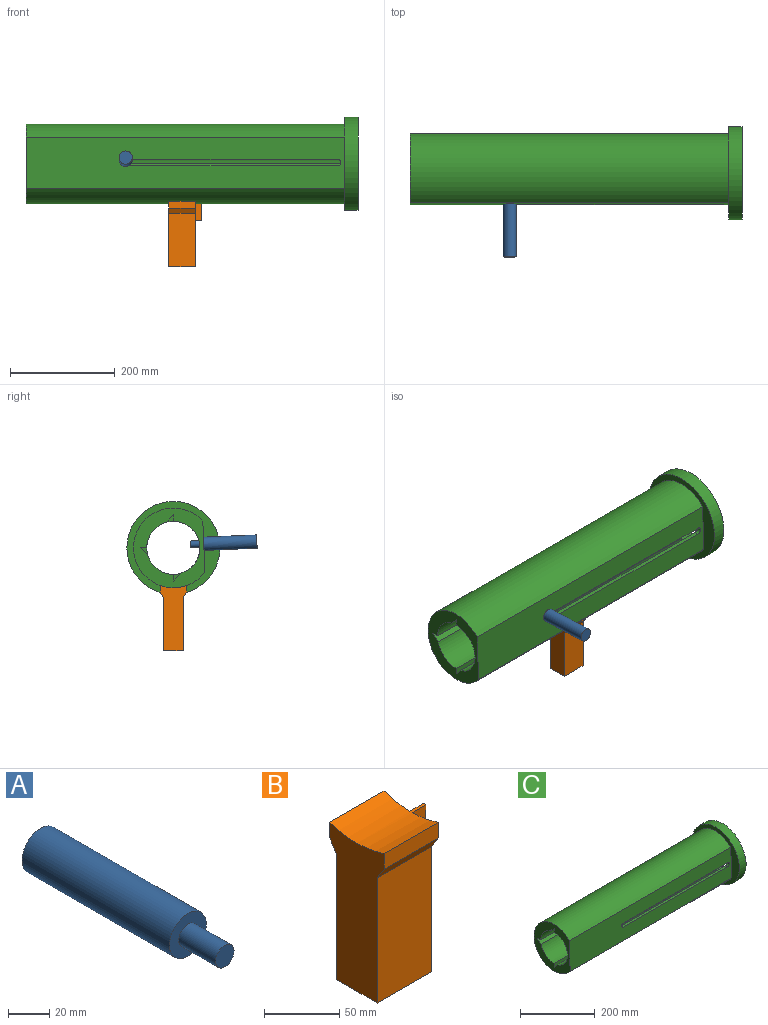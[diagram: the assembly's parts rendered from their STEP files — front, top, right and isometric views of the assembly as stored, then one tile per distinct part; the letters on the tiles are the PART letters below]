
ASSEMBLY  parts=3 mates=2
PART A: 5 faces, bbox 25.4x127x25.4 mm
  f0: plane 12.7x12.7mm, normal (0,-1,0), area 126.7mm2, adj f4
  f1: plane 25.4x25.4mm, normal (0,1,0), area 506.7mm2, adj f2
  f2: cylinder r=12.7mm len=101.6mm, axis (0,-1,0), area 8107.3mm2, adj f1,f3
  f3: plane 25.4x25.4mm, normal (0,-1,0), area 380mm2, adj f2,f4
  f4: cylinder r=6.35mm len=25.4mm, axis (0,-1,0), area 1013.4mm2, adj f0,f3
PART B: 14 faces, bbox 63.5x50.8x124.5 mm
  f0: plane 50.8x10.23mm, normal (0,0.85,-0.53), area 611.4mm2, adj f1,f7,f8,f9
  f1: plane 50.8x12.7mm, normal (0,1,0), area 645.2mm2, adj f0,f2,f8,f9
  f2: cylinder r=76.2mm len=63.5mm, axis (-1,0,0), area 2663.2mm2, adj f1,f3,f8,f9,f11,f12,f13
  f3: plane 50.8x12.7mm, normal (0,-1,0), area 645.2mm2, adj f2,f4,f8,f9
  f4: plane 50.8x10.23mm, normal (0,-0.85,-0.53), area 611.4mm2, adj f3,f5,f8,f9
  f5: plane 101.6x50.8mm, normal (0,-1,0), area 5161.3mm2, adj f4,f6,f8,f9
  f6: plane 50.8x38.1mm, normal (0,0,-1), area 1935.5mm2, adj f5,f7,f8,f9
  f7: plane 101.6x50.8mm, normal (0,1,0), area 5161.3mm2, adj f0,f6,f8,f9
  f8: plane 124.53x50.8mm, normal (1,0,0), area 4738.8mm2, adj f0,f1,f2,f3,f4,f5,f6,f7
  f9: plane 124.53x50.8mm, normal (-1,0,0), area 4822.2mm2, adj f0,f1,f2,f3,f4,f5,f6,f7
  f10: plane 12.7x2.54mm, normal (0,0,-1), area 32.3mm2, adj f8,f11,f12,f13
  f11: plane 32.81x12.7mm, normal (0,1,0), area 416.7mm2, adj f2,f8,f10,f13
  f12: plane 32.81x12.7mm, normal (0,-1,0), area 416.7mm2, adj f2,f8,f10,f13
  f13: plane 32.81x2.54mm, normal (1,0,0), area 83.3mm2, adj f2,f10,f11,f12
PART C: 20 faces, bbox 635x177.8x177.8 mm
  f0: cylinder r=50.8mm len=635mm, axis (-1,0,0), area 174256.3mm2, adj f3,f4,f5,f6,f7,f8,f9,f10
  f1: plane 609.6x97.78mm, normal (0,-1,0.04), area 54531mm2, adj f2,f9,f13,f16,f17,f18,f19
  f2: cylinder r=76.2mm len=609.6mm, axis (-1,0,0), area 227082.3mm2, adj f1,f9,f13
  f3: plane 609.6x12.7mm, normal (0,0,-1), area 7741.9mm2, adj f0,f4,f9,f10
  f4: plane 609.6x14.29mm, normal (0,-0.66,0.75), area 11612.9mm2, adj f0,f3,f9,f10
  f5: plane 609.6x12.7mm, normal (0,-1,0), area 7741.9mm2, adj f0,f6,f9,f11
  f6: plane 609.6x14.29mm, normal (0,0.75,0.66), area 11612.9mm2, adj f0,f5,f9,f11
  f7: plane 609.6x12.7mm, normal (0,1,0), area 7741.9mm2, adj f0,f8,f9,f12
  f8: plane 609.6x14.29mm, normal (0,-0.75,-0.66), area 11612.9mm2, adj f0,f7,f9,f12
  f9: plane 152.4x136.61mm, normal (-1,0,0), area 8713.7mm2, adj f0,f1,f2,f3,f4,f5,f6,f7
  f10: plane 14.29x12.6mm, normal (-1,0,0), area 76.6mm2, adj f0,f3,f4
  f11: plane 14.29x12.6mm, normal (-1,0,0), area 76.6mm2, adj f0,f5,f6
  f12: plane 14.29x12.6mm, normal (-1,0,0), area 76.6mm2, adj f0,f7,f8
  f13: plane 177.8x177.8mm, normal (-1,0,0), area 7777.8mm2, adj f1,f2,f14
  f14: cylinder r=88.9mm len=177.8mm, axis (-1,0,0), area 14187.8mm2, adj f13,f15
  f15: plane 177.8x177.8mm, normal (1,0,0), area 16721.3mm2, adj f0,f14
  f16: plane 393.7x8mm, normal (0,-0.04,-1), area 3154.2mm2, adj f0,f1,f17,f19
  f17: cylinder r=6.35mm len=13.03mm, axis (0,-1,0.04), area 155.8mm2, adj f0,f1,f16,f18
  f18: plane 393.7x8mm, normal (0,0.04,1), area 3154.2mm2, adj f0,f1,f17,f19
  f19: cylinder r=6.35mm len=13.03mm, axis (0,-1,0.04), area 155.8mm2, adj f0,f1,f16,f18
PLACE A rot(axis=(0.71,0.01,0.7),178.3deg) t=(190.64,-83.73,8.94)mm
PLACE B t=(273.05,-25.59,-70.77)mm
PLACE C t=(0,-25.59,1.07)mm fixed
MATE planar A.f2 <-> C.f1  axis (0,1,-0.04) through (190.64,-83.73,8.94)mm
MATE planar B.f2 <-> C.f0  axis (-1,0,0) through (304.8,-25.59,1.07)mm
